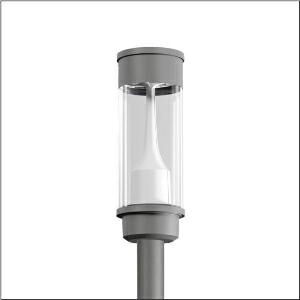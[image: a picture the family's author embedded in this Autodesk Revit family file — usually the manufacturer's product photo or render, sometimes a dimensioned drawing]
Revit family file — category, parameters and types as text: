
# Revit family: litepole_iq___pl1_2s_5xa5415cf14h_d917
name_source: partatom
category: Lighting Fixtures
units: mm (PartAtom-declared; Revit-internal decimal feet)

## family parameters
Cut with Voids When Loaded = No
Host = Face
Light Source = No
Part Type = Normal
Room Calculation Point = No
Round Connector Dimension = Use Diameter
Shared = No

## types (1)
- --- (1 x LED, 2970 lm, 23.9 W, 2200K)
    Apparent Load = 24 VA
    CIE Flux Codes = 23 62 94 96 100
    Color Rendering = 70
    Color Temperature = 2200K
    Default Elevation = 1800 mm
    Description = Litepole iQ, mast luminaire, Module 540 iQ-SR, primary light control with 3 zone facetted reflector, of plastic, silver coated, highly specular, structured, primary optical cover: cover, of PMMA, transparent, partly coated, light distribution: PL1.2s, light emission: direct distribution, primary light characteristic: symmetric, installation type: post-top, LED, High Power LED, rated luminous flux: 2.970lm, luminous efficacy: 124lm/W, light colour: 722, colour temperature: 2200K, control gear: ECG iQ, control: optimised constant luminous flux control (CLO 2.0), Desk-Remote (wireless, voltage-free reading and setting of iQ features in the workshop via application-optimized NFC function/RFID function), Light-Fading, Smart-Wire, Night-Set, Lumen-Switch, Temp-Guard, Auto-Match, Street-Remote, pre-setting: logarithmic dimming characteristic, with terminal, 6-pole, max. 2.5mm², mains connection: 230..240V, AC, 50/60Hz, start of lifetime: 24W, end of service life: 26W, reduction: 12W, luminaire housing, upper part, of glass-fibre reinforced polyester, coated, Siteco® metallic grey (DB 702S), diameter: 210mm, height: 590mm, spigot size: d x l = 76 x 70mm (post-top) | with reducer (optional accessory) 60 x 70mm, post-top mast mounting element, of diecast aluminium, coated, Siteco® metallic grey (DB 702S), Module 540 iQ-SR, traffic white (RAL 9016), equipment: standard, protection rating (complete): IP65, insulation class (complete): insulation class II (safety insulation), certification: CE, ENEC, VDE, packaging unit: 1 piece

Light Distribution: PL1.2s
    Height = 590 mm
    Lamp = 1 x LED
    Lamp Light Flux = 2970 lm
    Lamp Power = 23.9 W
    Lamp count = 1
    Length = 220 mm
    Luminous efficacy = 124 lm/W
    Manufacturer = Siteco
    ModVariant = No
    Model = 5XA5415CF14H
    Number of Poles = 1
    OnlyDefault = Yes
    Power Factor = 1
    Product Name = Litepole iQ | PL1.2s
    Product group = mast luminaire | pylon top
    ProductGroupID = 6100
    Protection Class = Protection class II
    Protection Degree = IP 65
    RLX_Detail_Level = 1
    RLX_Emergency_Light_Flux = 0 lm
    RLX_Emergency_Type = 0
    RLX_Emergency_Type_DB = No
    RlxData = <blob elided: 40221 chars, md5=0a97db9a>
    Socket = socket
    Standby Power = 0 W
    System Light Flux = 2970 lm
    System Power = 24 W
    Type Comments = factory setting: luminous flux: 100 % | dim-lin: 254 | 499 mA
    Type Image = l_1006025.jpg
    URL = http://relux.com
    VarID = @adj_114793
    Voltage = 0 V
    Weight = 0.00 kg
    Width = 0 mm  [stored 0 ft]

note: [stored X ft] marks values corroborated as IEEE doubles in the binary element streams (Revit-internal decimal feet)

## geometry (parser evidence)
native form markers: Blend x4, Sweep x11
no freeform markers — native parametric forms only
